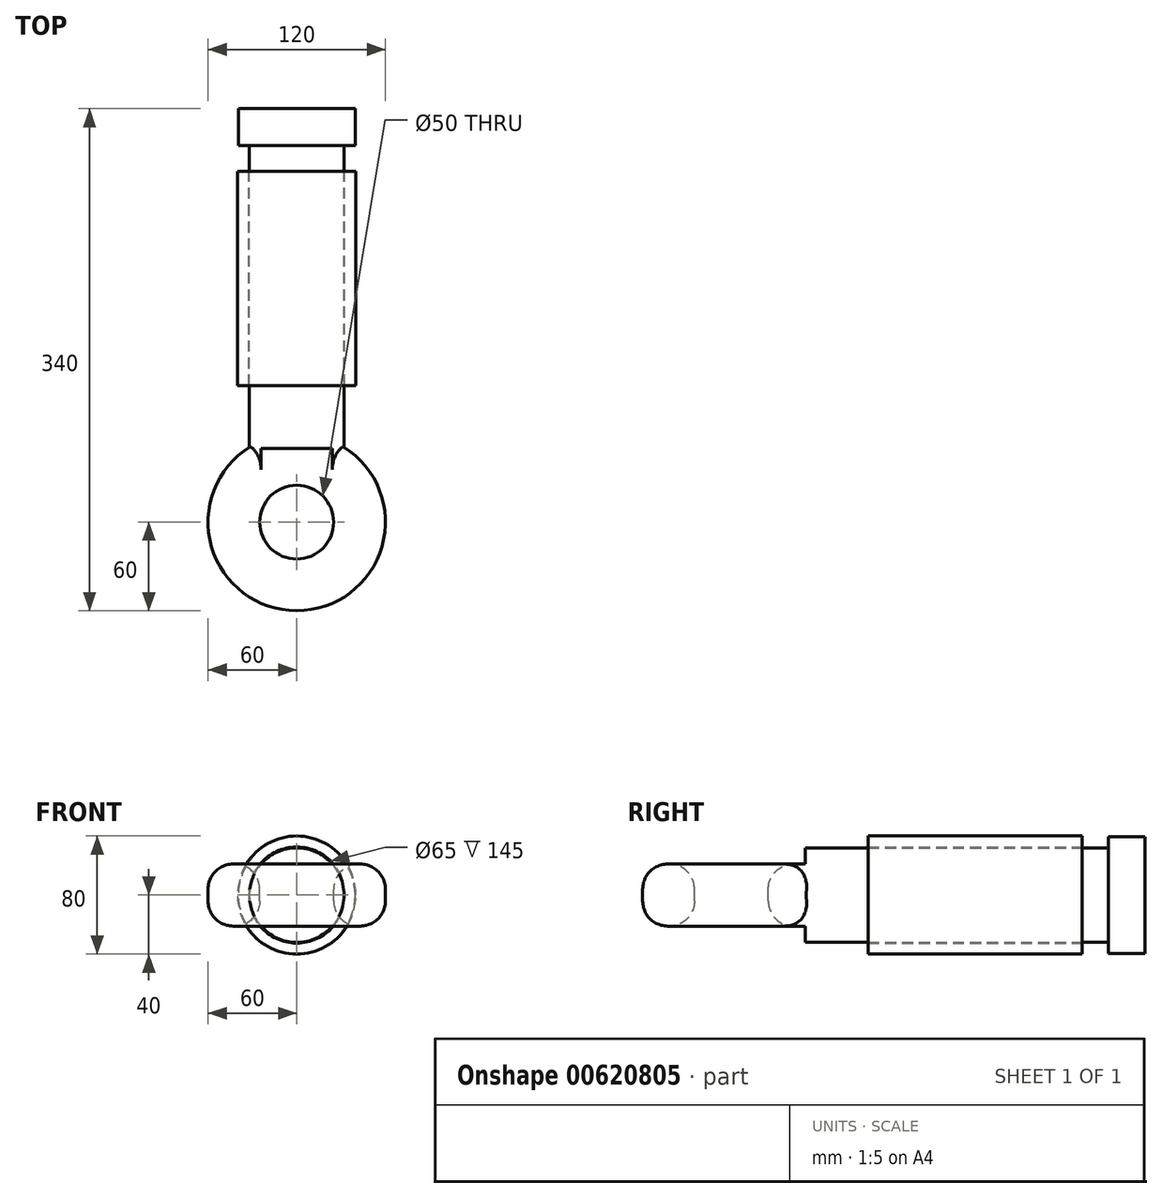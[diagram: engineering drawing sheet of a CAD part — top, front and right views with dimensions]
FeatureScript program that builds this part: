
annotation { "Feature Type Name" : "Feature", "Feature Type Description" : "" }
export const myFeature = defineFeature(function(context is Context, id is Id, definition is map)
    precondition{}
    {
        {
            var Q0;
            Q0=qCreatedBy(makeId("Front.planeOp"),FACE);
            var sketch = newSketch(context, id + "F0", { "sketchPlane" : qUnion([Q0])});
            skCircle(sketch, "E0", {"center": v(0, 0) * mm, "radius": 40 * mm});
            skCircle(sketch, "E1", {"center": v(0, 0) * mm, "radius": 32.5 * mm});
            skSolve(sketch);
        }
        {
            var Q0;
            Q0 = qSketchRegion(id + "F0", true);
            extrude(context, id + "F1", {"entities" : qUnion([Q0]), "endBound" : BoundingType.SYMMETRIC, "depth" : 145 * mm, "offsetDistance" : 25 * mm});
        }
        {
            var Q0;
            Q0=qCreatedBy(makeId("Front.planeOp"),FACE);
            var sketch = newSketch(context, id + "F2", { "sketchPlane" : qUnion([Q0])});
            skCircle(sketch, "E2", {"center": v(0, 0) * mm, "radius": 32 * mm});
            skSolve(sketch);
        }
        {
            var Q0;
            Q0 = qSketchRegion(id + "F2", true);
            extrude(context, id + "F3", {"entities" : qUnion([Q0]), "endBound" : BoundingType.SYMMETRIC, "depth" : 230 * mm, "offsetDistance" : 25 * mm});
        }
        {
            var Q0;
            Q0=qCreatedBy(makeId("Top.planeOp"),FACE);
            var sketch = newSketch(context, id + "F4", { "sketchPlane" : qUnion([Q0])});
            skCircle(sketch, "E3", {"center": v(0, -165) * mm, "radius": 60 * mm});
            skCircle(sketch, "E4", {"center": v(0, -165) * mm, "radius": 25 * mm});
            skSolve(sketch);
        }
        {
            var Q0;
            Q0 = qSketchRegion(id + "F4", true);
            extrude(context, id + "F5", {"entities" : qUnion([Q0]), "operationType" : NewBodyOperationType.ADD, "endBound" : BoundingType.SYMMETRIC, "oppositeDirection" : true, "depth" : 42 * mm, "offsetDistance" : 25 * mm});
        }
        {
            var Q0;
            Q0=makeQuery(id+"F5.opExtrude","CAP_EDGE",EDGE,{"disambiguationData":[OSD([sQuery(id+"F4.wireOp",EDGE,"E3")])],"isStart":false});
            var Q1;
            Q1=makeQuery(id+"F5.opExtrude","CAP_EDGE",EDGE,{"disambiguationData":[OSD([sQuery(id+"F4.wireOp",EDGE,"E4")])],"isStart":true});
            var Q2;
            Q2=makeQuery(id+"F5.opExtrude","CAP_EDGE",EDGE,{"disambiguationData":[OSD([sQuery(id+"F4.wireOp",EDGE,"E3")])],"isStart":true});
            var Q3;
            Q3=makeQuery(id+"F5.opExtrude","CAP_EDGE",EDGE,{"disambiguationData":[OSD([sQuery(id+"F4.wireOp",EDGE,"E4")])],"isStart":false});
            fillet(context, id + "F6", {"entities" : qUnion([Q0, Q1, Q2, Q3]), "radius" : 17 * mm, "tangentPropagation" : true, "allowEdgeOverflow" : false});
        }
        {
            var Q0;
            Q0=makeQuery(id+"F3.opExtrude","CAP_FACE",FACE,{"disambiguationData":[OSD([sQuery(id+"F2.wireOp",EDGE,"E2")])],"isStart":true});
            var sketch = newSketch(context, id + "F7", { "sketchPlane" : qUnion([Q0])});
            skCircle(sketch, "E5", {"center": v(0, 0) * mm, "radius": 39.5 * mm});
            skCircle(sketch, "E6", {"center": v(0, 0) * mm, "radius": 32 * mm});
            skSolve(sketch);
        }
        {
            var Q0;
            Q0 = qSketchRegion(id + "F7", true);
            extrude(context, id + "F8", {"entities" : qUnion([Q0]), "operationType" : NewBodyOperationType.ADD, "oppositeDirection" : true, "depth" : 25 * mm, "offsetDistance" : 25 * mm});
        }
    });
